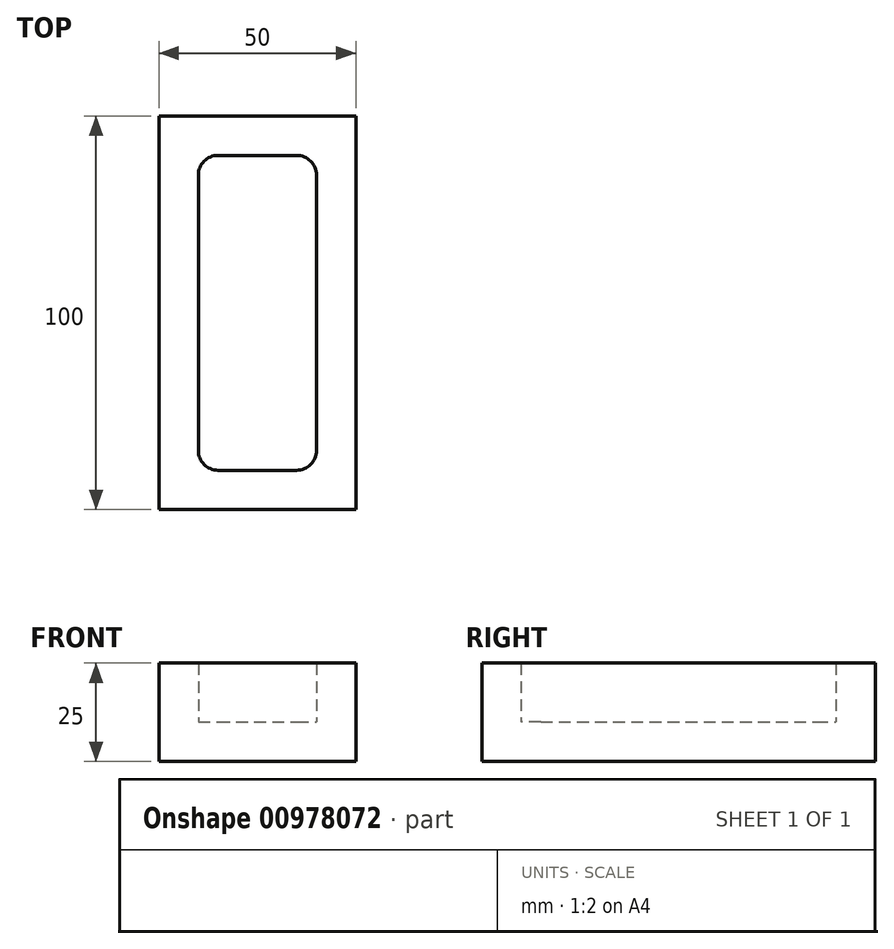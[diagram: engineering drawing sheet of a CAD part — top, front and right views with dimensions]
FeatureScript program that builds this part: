
annotation { "Feature Type Name" : "Feature", "Feature Type Description" : "" }
export const myFeature = defineFeature(function(context is Context, id is Id, definition is map)
    precondition{}
    {
        {
            var Q0;
            Q0=qCreatedBy(makeId("Top.planeOp"),FACE);
            var sketch = newSketch(context, id + "F0", { "sketchPlane" : qUnion([Q0])});
            skLineSegment(sketch, "E0.bottom", {"start": v(0, 0) * mm, "end": v(50, 0) * mm});
            skLineSegment(sketch, "E0.top", {"start": v(0, 100) * mm, "end": v(50, 100) * mm});
            skLineSegment(sketch, "E0.left", {"start": v(0, 0) * mm, "end": v(0, 100) * mm});
            skLineSegment(sketch, "E0.right", {"start": v(50, 0) * mm, "end": v(50, 100) * mm});
            skSolve(sketch);
        }
        {
            var Q0;
            Q0 = qSketchRegion(id + "F0", true);
            extrude(context, id + "F1", {"entities" : qUnion([Q0]), "depth" : 25 * mm, "offsetDistance" : 25 * mm});
        }
        {
            var Q0;
            Q0=makeQuery(id+"F1.opExtrude","CAP_FACE",FACE,{"disambiguationData":[OSD([sQuery(id+"F0.wireOp",EDGE,"E0.bottom"),sQuery(id+"F0.wireOp",EDGE,"E0.top"),sQuery(id+"F0.wireOp",EDGE,"E0.left"),sQuery(id+"F0.wireOp",EDGE,"E0.right")])],"isStart":false});
            shell(context, id + "F2", {"entities" : qUnion([Q0]), "thickness" : 10 * mm});
        }
        {
            var Q0;
            Q0=makeQuery(id+"F2.opShell","OFFSET_EDGE",EDGE,{"disambiguationData":[OSD([sQuery(id+"F0.wireOp",EDGE,"E0.top"),sQuery(id+"F0.wireOp",EDGE,"E0.left")])]});
            var Q1;
            Q1=makeQuery(id+"F2.opShell","OFFSET_EDGE",EDGE,{"disambiguationData":[OSD([sQuery(id+"F0.wireOp",EDGE,"E0.top"),sQuery(id+"F0.wireOp",EDGE,"E0.right")])]});
            var Q2;
            Q2=makeQuery(id+"F2.opShell","OFFSET_EDGE",EDGE,{"disambiguationData":[OSD([sQuery(id+"F0.wireOp",EDGE,"E0.bottom"),sQuery(id+"F0.wireOp",EDGE,"E0.right")])]});
            var Q3;
            Q3=makeQuery(id+"F2.opShell","OFFSET_EDGE",EDGE,{"disambiguationData":[OSD([sQuery(id+"F0.wireOp",EDGE,"E0.bottom"),sQuery(id+"F0.wireOp",EDGE,"E0.left")])]});
            fillet(context, id + "F3", {"entities" : qUnion([Q0, Q1, Q2, Q3]), "radius" : 5 * mm, "tangentPropagation" : true, "allowEdgeOverflow" : false});
        }
    });
